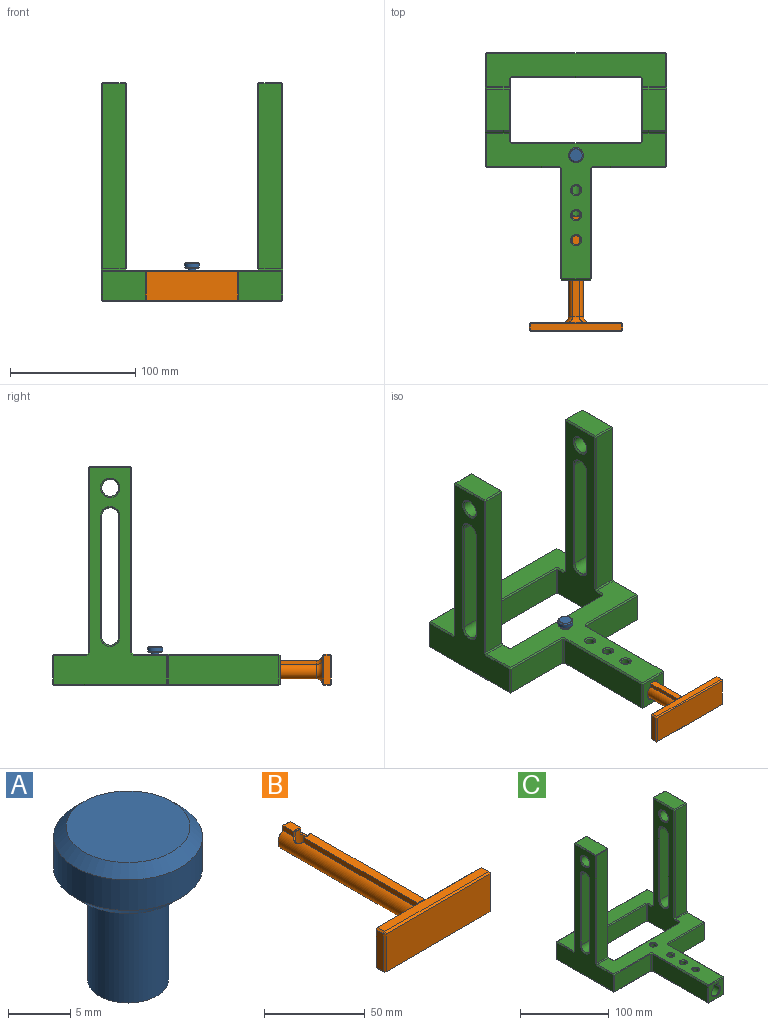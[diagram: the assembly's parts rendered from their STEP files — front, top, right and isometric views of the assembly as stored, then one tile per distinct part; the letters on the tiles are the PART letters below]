
ASSEMBLY  parts=3 mates=2
PART A: 8 faces, bbox 11.9x11.9x15 mm
  f0: cylinder r=3.25mm len=9.5mm, axis (0,0,1), area 194mm2, adj f1,f5
  f1: plane 6.5x6.5mm, normal (0,0,-1), area 33.2mm2, adj f0
  f2: cylinder r=5.97mm len=11.94mm, axis (0,0,-1), area 112.5mm2, adj f6,f7
  f3: plane 9.94x9.94mm, normal (0,0,1), area 77.6mm2, adj f7
  f4: plane 9.94x9.94mm, normal (0,0,-1), area 33.4mm2, adj f5,f6
  f5: cone r=3.75mm half-angle=45deg, axis (0,0,1), area 15.6mm2, adj f0,f4
  f6: cone r=5.97mm half-angle=45deg, axis (0,0,1), area 48.6mm2, adj f2,f4
  f7: cone r=4.97mm half-angle=45deg, axis (0,0,-1), area 48.6mm2, adj f2,f3
PART B: 52 faces, bbox 75x107x30.1 mm
  f0: cylinder r=6mm len=94.5mm, axis (0,1,0), area 2995mm2, adj f1,f2,f7,f8,f15,f39,f41,f42
  f1: plane 7.54x3.05mm, normal (1,0,0), area 23mm2, adj f0,f3,f46,f48
  f2: plane 7.54x3.05mm, normal (-1,0,0), area 23mm2, adj f0,f3,f43,f51
  f3: plane 7.69x5mm, normal (0,0,1), area 36.3mm2, adj f1,f2,f43,f45,f46,f49
  f4: plane 80.19x5mm, normal (0,0,1), area 398.8mm2, adj f7,f8,f18,f39,f40,f42
  f5: plane 32.51x23mm, normal (0,1,0), area 631.4mm2, adj f15,f16,f21,f25,f26
  f6: plane 13.5x11mm, normal (0,1,0), area 105.5mm2, adj f48,f49,f50,f51
  f7: plane 80.04x3.05mm, normal (1,0,0), area 243.8mm2, adj f0,f4,f16,f42
  f8: plane 80.04x3.05mm, normal (-1,0,0), area 243.8mm2, adj f0,f4,f17,f39
  f9: plane 32.51x23mm, normal (0,1,0), area 631.4mm2, adj f15,f17,f22,f23,f25
  f10: plane 23x5mm, normal (-1,0,0), area 115mm2, adj f23,f24,f30,f31
  f11: plane 74x5.06mm, normal (0,0,-1), area 370.2mm2, adj f12,f19,f21,f22,f30,f36
  f12: plane 24x5mm, normal (1,0,0), area 120mm2, adj f11,f26,f33,f37
  f13: plane 73x5mm, normal (0,0,1), area 365mm2, adj f24,f25,f32,f33
  f14: plane 73x23mm, normal (0,-1,0), area 1679mm2, adj f31,f32,f36,f37
  f15: torus R=11mm, axis (0,-1,0), area 311.1mm2, adj f0,f5,f9,f16,f17,f19
  f16: cylinder r=5mm len=7.3mm, axis (0,0,-1), area 29.9mm2, adj f5,f7,f15,f18,f25
  f17: cylinder r=5mm len=7.3mm, axis (0,0,1), area 29.9mm2, adj f8,f9,f15,f18,f25
  f18: cylinder r=5mm len=13.37mm, axis (1,0,0), area 64.6mm2, adj f4,f16,f17,f25
  f19: bspline ~7.98x1.04mm, area 10.8mm2, adj f11,f15,f21,f22
  f20: plane 1x1mm, normal (-0.58,0.58,0.58), area 0.9mm2, adj f23,f24,f25
  f21: plane 33.51x1mm, normal (0,0.71,-0.71), area 46.7mm2, adj f5,f11,f19,f26
  f22: plane 32.51x1mm, normal (0,0.71,-0.71), area 46mm2, adj f9,f11,f19,f27
  f23: plane 23x1mm, normal (-0.71,0.71,0), area 32.5mm2, adj f9,f10,f20,f27
  f24: plane 5x1mm, normal (-0.71,0,0.71), area 7.1mm2, adj f10,f13,f20,f28
  f25: plane 73.03x1.1mm, normal (0,0.71,0.71), area 104.6mm2, adj f5,f9,f13,f16,f17,f18,f20,f29
  f26: plane 24x1mm, normal (0.71,0.71,0), area 33.2mm2, adj f5,f12,f21,f29
  f27: plane 1x1mm, normal (-0.58,0.58,-0.58), area 0.9mm2, adj f22,f23,f30
  f28: plane 1x1mm, normal (-0.58,-0.58,0.58), area 0.9mm2, adj f24,f31,f32
  f29: plane 1x1mm, normal (0.58,0.58,0.58), area 0.9mm2, adj f25,f26,f33
  f30: plane 5x1mm, normal (-0.71,0,-0.71), area 7.1mm2, adj f10,f11,f27,f34
  f31: plane 23x1mm, normal (-0.71,-0.71,0), area 32.5mm2, adj f10,f14,f28,f34
  f32: plane 73x1mm, normal (0,-0.71,0.71), area 103.2mm2, adj f13,f14,f28,f35
  f33: plane 5x1mm, normal (0.71,0,0.71), area 7.1mm2, adj f12,f13,f29,f35
  f34: plane 1x1mm, normal (-0.58,-0.58,-0.58), area 0.9mm2, adj f30,f31,f36
  f35: plane 1x1mm, normal (0.58,-0.58,0.58), area 0.9mm2, adj f32,f33,f37
  f36: plane 74x1mm, normal (0,-0.71,-0.71), area 103.9mm2, adj f11,f14,f34,f37
  f37: plane 24x1mm, normal (0.71,-0.71,0), area 33.2mm2, adj f12,f14,f35,f36
  f38: cylinder r=3.5mm len=13.5mm, axis (0,0,1), area 231.6mm2, adj f39,f40,f41,f42,f43,f44,f45,f46
  f39: plane 3.4x0.77mm, normal (-0.5,0.87,0), area 2.6mm2, adj f0,f4,f8,f38,f40,f41
  f40: cone r=3.5mm half-angle=45deg, axis (0,0,1), area 3mm2, adj f4,f38,f39,f42
  f41: bspline ~6.93x2.61mm, area 7.2mm2, adj f0,f38,f39,f43
  f42: plane 3.4x0.77mm, normal (0.5,0.87,0), area 2.6mm2, adj f0,f4,f7,f38,f40,f44
  f43: plane 3.4x0.77mm, normal (-0.5,-0.87,0), area 2.6mm2, adj f0,f2,f3,f38,f41,f45
  f44: bspline ~6.93x2.61mm, area 7.2mm2, adj f0,f38,f42,f46
  f45: cone r=3.5mm half-angle=45deg, axis (0,0,1), area 3mm2, adj f3,f38,f43,f46
  f46: plane 3.4x0.77mm, normal (0.5,-0.87,0), area 2.6mm2, adj f0,f1,f3,f38,f44,f45
  f47: bspline ~8.73x8.01mm, area 20.9mm2, adj f0,f38
  f48: plane 3.39x0.51mm, normal (0.71,0.71,0), area 2.1mm2, adj f1,f6,f49,f50
  f49: plane 5x0.5mm, normal (0,0.71,0.71), area 3.2mm2, adj f3,f6,f48,f51
  f50: cone r=6mm half-angle=45deg, axis (0,-1,0), area 22.3mm2, adj f0,f6,f48,f51
  f51: plane 3.39x0.51mm, normal (-0.71,0.71,0), area 2.1mm2, adj f2,f6,f49,f50
PART C: 178 faces, bbox 145x182x175 mm
  f0: plane 173x90mm, normal (-1,0,0), area 5154.7mm2, adj f65,f66,f77,f78,f80,f81,f88,f100
  f1: plane 173x90mm, normal (1,0,0), area 5154.7mm2, adj f68,f69,f83,f84,f86,f87,f95,f102
  f2: plane 173x50mm, normal (1,0,0), area 4234.7mm2, adj f97,f98,f108,f114,f115,f122,f125,f126
  f3: plane 173x50mm, normal (-1,0,0), area 4234.7mm2, adj f105,f106,f113,f118,f119,f123,f128,f129
  f4: plane 143x116.5mm, normal (0,0,1), area 4703.5mm2, adj f49,f54,f59,f60,f63,f64,f70,f77
  f5: plane 143x26.5mm, normal (0,0,1), area 2884mm2, adj f82,f101,f102,f116,f117,f126,f127,f128
  f6: plane 180x143mm, normal (0,0,-1), area 9174mm2, adj f42,f46,f47,f51,f52,f56,f57,f66
  f7: plane 15.84x5.5mm, normal (0,0,-1), area 82mm2, adj f16,f17,f18,f40
  f8: plane 15.67x5.5mm, normal (0,0,-1), area 75.9mm2, adj f16,f17,f37,f40
  f9: plane 15.67x5.5mm, normal (0,0,-1), area 75.9mm2, adj f16,f17,f34,f37
  f10: plane 28.84x5.5mm, normal (0,0,-1), area 153.5mm2, adj f16,f17,f34,f144
  f11: plane 103x23mm, normal (0,1,0), area 2369mm2, adj f120,f125,f129,f130
  f12: plane 23x23mm, normal (0,-1,0), area 342.6mm2, adj f42,f45,f48,f49,f142,f143,f144,f145
  f13: plane 88x23mm, normal (1,0,0), area 2024mm2, adj f47,f48,f58,f59
  f14: plane 88x23mm, normal (-1,0,0), area 2024mm2, adj f45,f46,f54,f55
  f15: cylinder r=6.25mm len=89mm, axis (0,1,0), area 2988.2mm2, adj f16,f17,f18,f143
  f16: plane 89x3.14mm, normal (-1,0,0), area 279.2mm2, adj f7,f8,f9,f10,f15,f18,f35,f38
  f17: plane 89x3.14mm, normal (1,0,0), area 279.2mm2, adj f7,f8,f9,f10,f15,f18,f33,f36
  f18: plane 15x12.5mm, normal (0,-1,0), area 137.6mm2, adj f7,f15,f16,f17
  f19: plane 58x23mm, normal (0,-1,0), area 1334mm2, adj f55,f56,f64,f65
  f20: plane 58x23mm, normal (0,-1,0), area 1334mm2, adj f57,f58,f69,f70
  f21: plane 143x23mm, normal (0,1,0), area 3289mm2, adj f67,f81,f82,f83
  f22: plane 103x23mm, normal (0,-1,0), area 2369mm2, adj f127,f136,f137,f141
  f23: plane 148x18mm, normal (0,1,0), area 2664mm2, adj f99,f100,f115,f116
  f24: plane 148x18mm, normal (0,-1,0), area 2664mm2, adj f78,f79,f96,f97
  f25: plane 33x18mm, normal (0,0,1), area 594mm2, adj f79,f80,f98,f99
  f26: plane 148x18mm, normal (0,1,0), area 2664mm2, adj f103,f104,f117,f118
  f27: plane 148x18mm, normal (0,-1,0), area 2664mm2, adj f85,f86,f106,f107
  f28: plane 33x18mm, normal (0,0,1), area 594mm2, adj f84,f85,f104,f105
  f29: cylinder r=6.75mm len=18mm, axis (1,0,0), area 763.4mm2, adj f147,f149
  f30: cylinder r=6.75mm len=18mm, axis (1,0,0), area 763.4mm2, adj f146,f148
  f31: cylinder r=3.5mm len=9mm, axis (0,0,1), area 197.9mm2, adj f32,f153
  f32: plane 7x7mm, normal (0,0,1), area 38.5mm2, adj f31
  f33: plane 4.33x0.75mm, normal (0,0,1), area 2.2mm2, adj f17,f34
  f34: cylinder r=3.5mm len=7mm, axis (0,0,1), area 88mm2, adj f9,f10,f33,f35,f150
  f35: plane 4.33x0.75mm, normal (0,0,1), area 2.2mm2, adj f16,f34
  f36: plane 4.33x0.75mm, normal (0,0,1), area 2.2mm2, adj f17,f37
  f37: cylinder r=3.5mm len=7mm, axis (0,0,1), area 88mm2, adj f8,f9,f36,f38,f151
  f38: plane 4.33x0.75mm, normal (0,0,1), area 2.2mm2, adj f16,f37
  f39: plane 4.33x0.75mm, normal (0,0,1), area 2.2mm2, adj f17,f40
  f40: cylinder r=3.5mm len=7mm, axis (0,0,1), area 88mm2, adj f7,f8,f39,f41,f152
  f41: plane 4.33x0.75mm, normal (0,0,1), area 2.2mm2, adj f16,f40
  f42: plane 23x1mm, normal (0,-0.71,-0.71), area 32.5mm2, adj f6,f12,f43,f44
  f43: plane 1x1mm, normal (-0.58,-0.58,-0.58), area 0.9mm2, adj f42,f45,f46
  f44: plane 1x1mm, normal (0.58,-0.58,-0.58), area 0.9mm2, adj f42,f47,f48
  f45: plane 23x1mm, normal (-0.71,-0.71,0), area 32.5mm2, adj f12,f14,f43,f50
  f46: plane 88x1mm, normal (-0.71,0,-0.71), area 124.5mm2, adj f6,f14,f43,f51
  f47: plane 88x1mm, normal (0.71,0,-0.71), area 124.5mm2, adj f6,f13,f44,f52
  f48: plane 23x1mm, normal (0.71,-0.71,0), area 32.5mm2, adj f12,f13,f44,f53
  f49: plane 23x1mm, normal (0,-0.71,0.71), area 32.5mm2, adj f4,f12,f50,f53
  f50: plane 1x1mm, normal (-0.58,-0.58,0.58), area 0.9mm2, adj f45,f49,f54
  f51: plane 2x2mm, normal (-0.58,-0.58,-0.58), area 2.6mm2, adj f6,f46,f55,f56
  f52: plane 2x2mm, normal (0.58,-0.58,-0.58), area 2.6mm2, adj f6,f47,f57,f58
  f53: plane 1x1mm, normal (0.58,-0.58,0.58), area 0.9mm2, adj f48,f49,f59
  f54: plane 88x1mm, normal (-0.71,0,0.71), area 124.5mm2, adj f4,f14,f50,f60
  f55: plane 23x1mm, normal (-0.71,-0.71,0), area 32.5mm2, adj f14,f19,f51,f60
  f56: plane 58x1mm, normal (0,-0.71,-0.71), area 82mm2, adj f6,f19,f51,f61
  f57: plane 58x1mm, normal (0,-0.71,-0.71), area 82mm2, adj f6,f20,f52,f62
  f58: plane 23x1mm, normal (0.71,-0.71,0), area 32.5mm2, adj f13,f20,f52,f63
  f59: plane 88x1mm, normal (0.71,0,0.71), area 124.5mm2, adj f4,f13,f53,f63
  f60: plane 2x2mm, normal (-0.58,-0.58,0.58), area 2.6mm2, adj f4,f54,f55,f64
  f61: plane 1x1mm, normal (-0.58,-0.58,-0.58), area 0.9mm2, adj f56,f65,f66
  f62: plane 1x1mm, normal (0.58,-0.58,-0.58), area 0.9mm2, adj f57,f68,f69
  f63: plane 2x2mm, normal (0.58,-0.58,0.58), area 2.6mm2, adj f4,f58,f59,f70
  f64: plane 58x1mm, normal (0,-0.71,0.71), area 82mm2, adj f4,f19,f60,f71
  f65: plane 23x1mm, normal (-0.71,-0.71,0), area 32.5mm2, adj f0,f19,f61,f71
  f66: plane 90x1mm, normal (-0.71,0,-0.71), area 127.3mm2, adj f0,f6,f61,f73
  f67: plane 143x1mm, normal (0,0.71,-0.71), area 202.2mm2, adj f6,f21,f73,f74
  f68: plane 90x1mm, normal (0.71,0,-0.71), area 127.3mm2, adj f1,f6,f62,f74
  f69: plane 23x1mm, normal (0.71,-0.71,0), area 32.5mm2, adj f1,f20,f62,f76
  f70: plane 58x1mm, normal (0,-0.71,0.71), area 82mm2, adj f4,f20,f63,f76
  f71: plane 1x1mm, normal (-0.58,-0.58,0.58), area 0.9mm2, adj f64,f65,f77
  f72: plane 1x1mm, normal (-0.58,-0.58,0.58), area 0.9mm2, adj f78,f79,f80
  f73: plane 1x1mm, normal (-0.58,0.58,-0.58), area 0.9mm2, adj f66,f67,f81
  f74: plane 1x1mm, normal (0.58,0.58,-0.58), area 0.9mm2, adj f67,f68,f83
  f75: plane 1x1mm, normal (0.58,-0.58,0.58), area 0.9mm2, adj f84,f85,f86
  f76: plane 1x1mm, normal (0.58,-0.58,0.58), area 0.9mm2, adj f69,f70,f87
  f77: plane 26.5x1mm, normal (-0.71,0,0.71), area 37.5mm2, adj f0,f4,f71,f88
  f78: plane 148x1mm, normal (-0.71,-0.71,0), area 209.3mm2, adj f0,f24,f72,f88
  f79: plane 18x1mm, normal (0,-0.71,0.71), area 25.5mm2, adj f24,f25,f72,f89
  f80: plane 33x1mm, normal (-0.71,0,0.71), area 46.7mm2, adj f0,f25,f72,f90
  f81: plane 23x1mm, normal (-0.71,0.71,0), area 32.5mm2, adj f0,f21,f73,f91
  f82: plane 143x1mm, normal (0,0.71,0.71), area 202.2mm2, adj f5,f21,f91,f92
  f83: plane 23x1mm, normal (0.71,0.71,0), area 32.5mm2, adj f1,f21,f74,f92
  f84: plane 33x1mm, normal (0.71,0,0.71), area 46.7mm2, adj f1,f28,f75,f93
  f85: plane 18x1mm, normal (0,-0.71,0.71), area 25.5mm2, adj f27,f28,f75,f94
  f86: plane 148x1mm, normal (0.71,-0.71,0), area 209.3mm2, adj f1,f27,f75,f95
  f87: plane 26.5x1mm, normal (0.71,0,0.71), area 37.5mm2, adj f1,f4,f76,f95
  f88: plane 2x2mm, normal (-0.58,-0.58,0.58), area 2.6mm2, adj f0,f77,f78,f96
  f89: plane 1x1mm, normal (0.58,-0.58,0.58), area 0.9mm2, adj f79,f97,f98
  f90: plane 1x1mm, normal (-0.58,0.58,0.58), area 0.9mm2, adj f80,f99,f100
  f91: plane 1x1mm, normal (-0.58,0.58,0.58), area 0.9mm2, adj f81,f82,f101
  f92: plane 1x1mm, normal (0.58,0.58,0.58), area 0.9mm2, adj f82,f83,f102
  f93: plane 1x1mm, normal (0.58,0.58,0.58), area 0.9mm2, adj f84,f103,f104
  f94: plane 1x1mm, normal (-0.58,-0.58,0.58), area 0.9mm2, adj f85,f105,f106
  f95: plane 2x2mm, normal (0.58,-0.58,0.58), area 2.6mm2, adj f1,f86,f87,f107
  f96: plane 18x1mm, normal (0,-0.71,0.71), area 25.5mm2, adj f4,f24,f88,f108
  f97: plane 148x1mm, normal (0.71,-0.71,0), area 209.3mm2, adj f2,f24,f89,f108
  f98: plane 33x1mm, normal (0.71,0,0.71), area 46.7mm2, adj f2,f25,f89,f109
  f99: plane 18x1mm, normal (0,0.71,0.71), area 25.5mm2, adj f23,f25,f90,f109
  f100: plane 148x1mm, normal (-0.71,0.71,0), area 209.3mm2, adj f0,f23,f90,f110
  f101: plane 26.5x1mm, normal (-0.71,0,0.71), area 37.5mm2, adj f0,f5,f91,f110
  f102: plane 26.5x1mm, normal (0.71,0,0.71), area 37.5mm2, adj f1,f5,f92,f111
  f103: plane 148x1mm, normal (0.71,0.71,0), area 209.3mm2, adj f1,f26,f93,f111
  f104: plane 18x1mm, normal (0,0.71,0.71), area 25.5mm2, adj f26,f28,f93,f112
  f105: plane 33x1mm, normal (-0.71,0,0.71), area 46.7mm2, adj f3,f28,f94,f112
  f106: plane 148x1mm, normal (-0.71,-0.71,0), area 209.3mm2, adj f3,f27,f94,f113
  f107: plane 18x1mm, normal (0,-0.71,0.71), area 25.5mm2, adj f4,f27,f95,f113
  f108: plane 2x2mm, normal (0.58,-0.58,0.58), area 2.6mm2, adj f2,f96,f97,f114
  f109: plane 1x1mm, normal (0.58,0.58,0.58), area 0.9mm2, adj f98,f99,f115
  f110: plane 2x2mm, normal (-0.58,0.58,0.58), area 2.6mm2, adj f0,f100,f101,f116
  f111: plane 2x2mm, normal (0.58,0.58,0.58), area 2.6mm2, adj f1,f102,f103,f117
  f112: plane 1x1mm, normal (-0.58,0.58,0.58), area 0.9mm2, adj f104,f105,f118
  f113: plane 2x2mm, normal (-0.58,-0.58,0.58), area 2.6mm2, adj f3,f106,f107,f119
  f114: plane 6.5x1mm, normal (0.71,0,0.71), area 9.2mm2, adj f2,f4,f108,f121
  f115: plane 148x1mm, normal (0.71,0.71,0), area 209.3mm2, adj f2,f23,f109,f122
  f116: plane 18x1mm, normal (0,0.71,0.71), area 25.5mm2, adj f5,f23,f110,f122
  f117: plane 18x1mm, normal (0,0.71,0.71), area 25.5mm2, adj f5,f26,f111,f123
  f118: plane 148x1mm, normal (-0.71,0.71,0), area 209.3mm2, adj f3,f26,f112,f123
  f119: plane 6.5x1mm, normal (-0.71,0,0.71), area 9.2mm2, adj f3,f4,f113,f124
  f120: plane 103x1mm, normal (0,0.71,0.71), area 145.7mm2, adj f4,f11,f121,f124
  f121: plane 2x2mm, normal (0.58,0.58,0.58), area 2.6mm2, adj f4,f114,f120,f125
  f122: plane 2x2mm, normal (0.58,0.58,0.58), area 2.6mm2, adj f2,f115,f116,f126
  f123: plane 2x2mm, normal (-0.58,0.58,0.58), area 2.6mm2, adj f3,f117,f118,f128
  f124: plane 2x2mm, normal (-0.58,0.58,0.58), area 2.6mm2, adj f4,f119,f120,f129
  f125: plane 23x1mm, normal (0.71,0.71,0), area 32.5mm2, adj f2,f11,f121,f131
  f126: plane 6.5x1mm, normal (0.71,0,0.71), area 9.2mm2, adj f2,f5,f122,f132
  f127: plane 103x1mm, normal (0,-0.71,0.71), area 145.7mm2, adj f5,f22,f132,f133
  f128: plane 6.5x1mm, normal (-0.71,0,0.71), area 9.2mm2, adj f3,f5,f123,f133
  f129: plane 23x1mm, normal (-0.71,0.71,0), area 32.5mm2, adj f3,f11,f124,f134
  f130: plane 103x1mm, normal (0,0.71,-0.71), area 145.7mm2, adj f6,f11,f131,f134
  f131: plane 2x2mm, normal (0.58,0.58,-0.58), area 2.6mm2, adj f6,f125,f130,f135
  f132: plane 2x2mm, normal (0.58,-0.58,0.58), area 2.6mm2, adj f5,f126,f127,f136
  f133: plane 2x2mm, normal (-0.58,-0.58,0.58), area 2.6mm2, adj f5,f127,f128,f137
  f134: plane 2x2mm, normal (-0.58,0.58,-0.58), area 2.6mm2, adj f6,f129,f130,f138
  f135: plane 50x1mm, normal (0.71,0,-0.71), area 70.7mm2, adj f2,f6,f131,f139
  f136: plane 23x1mm, normal (0.71,-0.71,0), area 32.5mm2, adj f2,f22,f132,f139
  f137: plane 23x1mm, normal (-0.71,-0.71,0), area 32.5mm2, adj f3,f22,f133,f140
  f138: plane 50x1mm, normal (-0.71,0,-0.71), area 70.7mm2, adj f3,f6,f134,f140
  f139: plane 2x2mm, normal (0.58,-0.58,-0.58), area 2.6mm2, adj f6,f135,f136,f141
  f140: plane 2x2mm, normal (-0.58,-0.58,-0.58), area 2.6mm2, adj f6,f137,f138,f141
  f141: plane 103x1mm, normal (0,-0.71,-0.71), area 145.7mm2, adj f6,f22,f139,f140
  f142: plane 4.14x1mm, normal (-0.71,-0.71,0), area 4.7mm2, adj f12,f16,f143,f144
  f143: cone r=7.25mm half-angle=45deg, axis (0,-1,0), area 50.4mm2, adj f12,f15,f142,f145
  f144: plane 7.5x1mm, normal (0,-0.71,-0.71), area 9.2mm2, adj f10,f12,f142,f145
  f145: plane 4.14x1mm, normal (0.71,-0.71,0), area 4.7mm2, adj f12,f17,f143,f144
  f146: cone r=6.75mm half-angle=45deg, axis (-1,0,0), area 64.4mm2, adj f3,f30
  f147: cone r=7.75mm half-angle=45deg, axis (1,0,0), area 64.4mm2, adj f2,f29
  f148: cone r=6.75mm half-angle=45deg, axis (1,0,0), area 64.4mm2, adj f1,f30
  f149: cone r=6.75mm half-angle=45deg, axis (-1,0,0), area 64.4mm2, adj f0,f29
  f150: cone r=3.5mm half-angle=45deg, axis (0,0,1), area 35.5mm2, adj f4,f34
  f151: cone r=3.5mm half-angle=45deg, axis (0,0,1), area 35.5mm2, adj f4,f37
  f152: cone r=3.5mm half-angle=45deg, axis (0,0,1), area 35.5mm2, adj f4,f40
  f153: cone r=3.5mm half-angle=45deg, axis (0,0,1), area 35.5mm2, adj f4,f31
  f154: plane 96.25x18mm, normal (0,1,0), area 1732.5mm2, adj f155,f157,f168,f174
  f155: cylinder r=6.75mm len=18mm, axis (1,0,0), area 381.7mm2, adj f154,f156,f169,f175
  f156: plane 96.25x18mm, normal (0,-1,0), area 1732.5mm2, adj f155,f157,f167,f177
  f157: cylinder r=6.75mm len=18mm, axis (1,0,0), area 381.7mm2, adj f154,f156,f166,f176
  f158: cylinder r=6.75mm len=18mm, axis (1,0,0), area 381.7mm2, adj f159,f161,f162,f171
  f159: plane 96.25x18mm, normal (0,-1,0), area 1732.5mm2, adj f158,f160,f163,f173
  f160: cylinder r=6.75mm len=18mm, axis (1,0,0), area 381.7mm2, adj f159,f161,f165,f172
  f161: plane 96.25x18mm, normal (0,1,0), area 1732.5mm2, adj f158,f160,f164,f170
  f162: cone r=7.75mm half-angle=45deg, axis (-1,0,0), area 32.2mm2, adj f0,f158,f163,f164
  f163: plane 96.25x1mm, normal (-0.71,-0.71,0), area 136.1mm2, adj f0,f159,f162,f165
  f164: plane 96.25x1mm, normal (-0.71,0.71,0), area 136.1mm2, adj f0,f161,f162,f165
  f165: cone r=7.75mm half-angle=45deg, axis (-1,0,0), area 32.2mm2, adj f0,f160,f163,f164
  f166: cone r=7.75mm half-angle=45deg, axis (-1,0,0), area 32.2mm2, adj f3,f157,f167,f168
  f167: plane 96.25x1mm, normal (-0.71,-0.71,0), area 136.1mm2, adj f3,f156,f166,f169
  f168: plane 96.25x1mm, normal (-0.71,0.71,0), area 136.1mm2, adj f3,f154,f166,f169
  f169: cone r=7.75mm half-angle=45deg, axis (-1,0,0), area 32.2mm2, adj f3,f155,f167,f168
  f170: plane 96.25x1mm, normal (0.71,0.71,0), area 136.1mm2, adj f2,f161,f171,f172
  f171: cone r=6.75mm half-angle=45deg, axis (1,0,0), area 32.2mm2, adj f2,f158,f170,f173
  f172: cone r=6.75mm half-angle=45deg, axis (1,0,0), area 32.2mm2, adj f2,f160,f170,f173
  f173: plane 96.25x1mm, normal (0.71,-0.71,0), area 136.1mm2, adj f2,f159,f171,f172
  f174: plane 96.25x1mm, normal (0.71,0.71,0), area 136.1mm2, adj f1,f154,f175,f176
  f175: cone r=7.75mm half-angle=45deg, axis (1,0,0), area 32.2mm2, adj f1,f155,f174,f177
  f176: cone r=7.75mm half-angle=45deg, axis (1,0,0), area 32.2mm2, adj f1,f157,f174,f177
  f177: plane 96.25x1mm, normal (0.71,-0.71,0), area 136.1mm2, adj f1,f156,f175,f176
PLACE A rot(axis=(0,0,1),107.7deg) t=(9.53,29.76,0.93)mm
PLACE B t=(0,-7.26,0)mm
PLACE C t=(0,16.73,0)mm fixed
MATE cylindrical B.f0 <-> C.f15  axis (0,1,0) through (0,-7.26,0)mm
MATE cylindrical C.f153 <-> A.f6  axis (0,0,1) through (0,26.73,13.75)mm
